# Revit family: Haworth_Masters_VerticalStorage
name_source: partatom
category: Furniture Systems
revit_build: Autodesk Revit 2018 (Build: 20170223_1515(x64)
units: mm (PartAtom-declared; Revit-internal decimal feet)

## family parameters
Always vertical = Yes
Cut with Voids When Loaded = No
OmniClass Number = 23.40.70.14.64.21
OmniClass Title = Systems Furniture
Part Type = Normal
Room Calculation Point = No
Round Connector Dimension = Use Diameter
Shared = No
Work Plane-Based = No

## types (3) — shared parameters
# of Doors = 6
2nd Pair Start = 32 3/32"
Actual # of Doors = 6
Actual Depth = 14"
Actual One High = 12 13/16"
Actual Width = 96"
Assembly Code = E2020200
Cabinet Finish = Haworth _ Wood _ White Oak
Custom Size = No
Dbl Door Size = 31 13/16"
Description = Haworth - Masters - Vertical Storage
Divider 1 = Yes
Divider 1 Location = 32"
Divider 2 = Yes
Divider 2 Location = 32"
Door Finish = Haworth _ Wood _ White Oak
Door Height = 26 5/8"
Door Width = 15 27/32"
Glass Doors = No
Glass Finish = Haworth _ Glass _ Clear
Legal Depth = No
Letter Depth = Yes
Manufacturer = Haworth
Max. Width = 96"
Min. Width = 30"
Model = Haworth - Masters - Vertical Storage
One High = No
Preliminary Doors = 6
Revision Number = 3
Size = Verify Final Dim. w/ Haworth
Sliding Door Width = 31 15/16"
Standard Widths = 30-96 in. @ 6 in. increments
Sustainability Info = http://www.haworth.com
Two High = Yes
Two High One Divider = Yes
Two High Two Divider = Yes
URL = www.haworth.com
URL - Product = http://www.haworth.com
Warranty = http://www.haworth.com
Width = 96"

## per-type parameters (varying)
| type | 1 Door | 2 doors | 3_4 Doors | 6 Doors | Actual Height | Actual Hinged Doors | Open | Overhead | Solid Doors | Vertical Storage |
| Hinged Doors | Yes | Yes | Yes | Yes | 28 7/8" | Yes | No | Yes | Yes | No |
| Open | No | No | No | No | 52 1/2" | No | Yes | No | No | Yes |
| Sliding Door | No | No | No | No | 52 1/2" | Yes | No | No | Yes | Yes |

type visibility flags (boolean, named after types; folded from table):
- Hinged Doors: Yes: Hinged Doors
- Open: Yes: Hinged Doors
- Sliding Door: Yes: Sliding Door

## geometry (parser evidence)
native form markers: Sweep x9
no freeform markers — native parametric forms only
